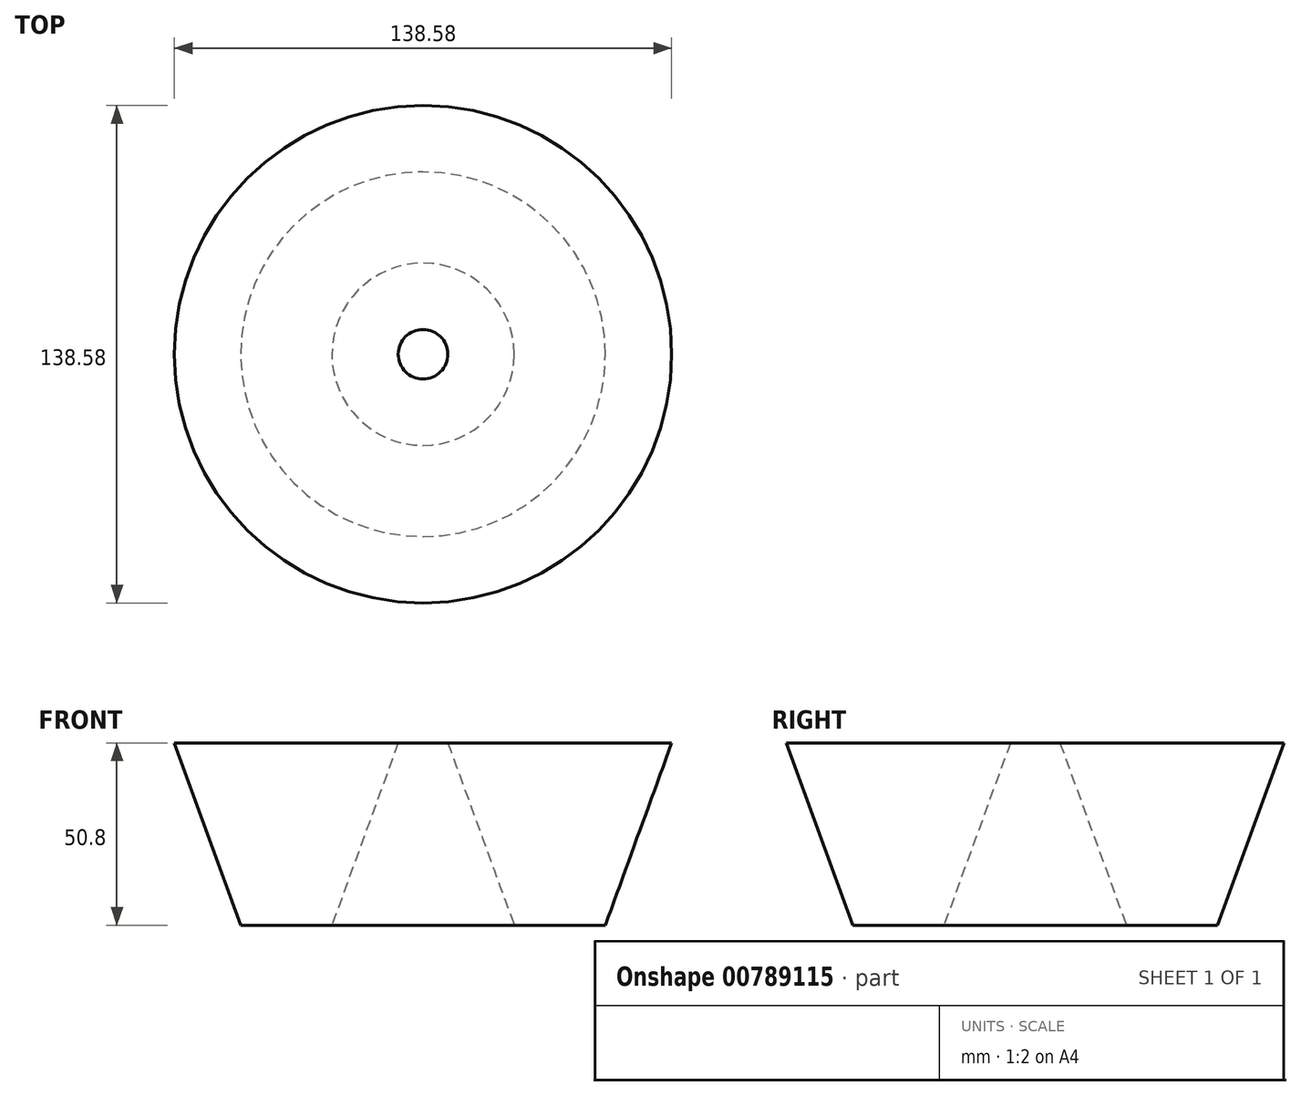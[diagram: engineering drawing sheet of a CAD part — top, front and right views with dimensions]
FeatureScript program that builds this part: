
annotation { "Feature Type Name" : "Feature", "Feature Type Description" : "" }
export const myFeature = defineFeature(function(context is Context, id is Id, definition is map)
    precondition{}
    {
        {
            var Q0;
            Q0=qCreatedBy(makeId("Top.planeOp"),FACE);
            var sketch = newSketch(context, id + "F0", { "sketchPlane" : qUnion([Q0])});
            skCircle(sketch, "E0", {"center": v(0, 0) * mm, "radius": 50.8 * mm});
            skCircle(sketch, "E1", {"center": v(0, 0) * mm, "radius": 25.4 * mm});
            skSolve(sketch);
        }
        {
            var Q0;
            Q0 = qSketchRegion(id + "F0", true);
            extrude(context, id + "F1", {"entities" : qUnion([Q0]), "depth" : 50.8 * mm, "offsetDistance" : 25.4 * mm, "hasDraft" : true, "draftAngle" : 20 * degree});
        }
    });
